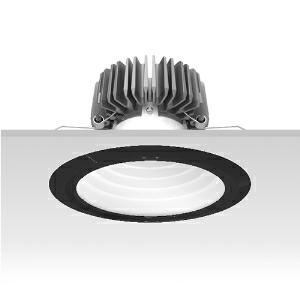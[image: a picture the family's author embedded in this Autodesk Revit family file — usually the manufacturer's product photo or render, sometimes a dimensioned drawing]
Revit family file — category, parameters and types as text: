
# Revit family: 3f_filippi_-_3f_reno_bianco_ampio_3f_filippi_-_30625_a01026_-_3f_reno_200_wh_2000-930_wide___vt_bk_0df5
name_source: partatom
category: Lighting Fixtures
units: mm (PartAtom-declared; Revit-internal decimal feet)

## family parameters
Cut with Voids When Loaded = No
Host = Face
Light Source = No
Part Type = Normal
Room Calculation Point = No
Round Connector Dimension = Use Diameter
Shared = No

## types (1)
- 3F Filippi - 3F Reno Bianco Ampio (1 x LED, 1804 lm, 24 W, 3000 K)
    Apparent Load = 24 VA
    Approval mark = CE
    CIE Flux Codes = 75 94 99 100 100
    Color Rendering = 90
    Color Temperature = 3000 K
    Control Gear = Electronic ballast
    Default Elevation = 1800 mm
    Description = ILLUMINOTECHNICAL
Luminous efficiency 100% (DLOR 100%, ULOR 0%).
Initial luminous flux of the luminaire 1804 lm.
Direct symmetric wide distribution.
Installation Interdistance Transv.D = 1.56 x hu - Long.D = 1.56 x hu.
Average luminance <3000 cd/m² for radial angles >65°.
Tabular UGR (CIE 117 - 4H-8H; S=0.25H; 70/50/20): RUG 20.6 - 20.5.
Beam angle: 74° - 74°.
Luminous efficacy 75 lm/W.
Lifetime (L90/B10): 30000 h. (tq+25°C)
Lifetime (L85/B10): 50000 h. (tq+25°C)
Lifetime (L70/B10): 80000 h. (tq+25°C)
Sudden decreased luminous flux after 50000 hours: 0% (C0).
Photobiological safety in compliance with IEC/TR 62778: RG0 risk exempt, (IEC 62471).
In compliance with IEC/EN 62722-2-1 - IEC/EN 62717 standards.

SOURCE
Compact LED module 2000/930.
Energy efficiency class (UE 2019/2020 - UE 2019/2015): E.
CIE 13.3 Colour rendering index: CRI >90 (R9 >50%).
IES TM-30 Fidelity Index: Rf = 92 Rg = 101.
CCT nominal colour temperature 3000 K.
Colour initial tolerance (MacAdam): SDCM 3.
Zhaga Book 3 compliant.

MECHANICAL
Passive heat dissipator in die-casting aluminium, oversized, for optimum thermal management of the LED module.
Parabolic element with graduated/concentric rings in white polycarbonate.
Transparent external lens with glossy and satin differentiated surfaces, with a cooling and anti-insect system in methacrylate (PMMA).
Fastening spring clips in stainless steel.
Dimensions: diameter 226 mm, height 146 mm. Weight 1.07 kg.
IP44 protection degree for exposed part, IP20 for recessed part.
Mechanical strength to impacts IK06 (1 joule).
Glow-wire test resistance 650°C.

ELECTRICAL
Wiring on a separate unit.
Halogen Free electronic wiring 230V-50/60Hz, power factor 0.95, THD <25%, constant output current, SELV, class II, 1 driver.
Power of the luminaire 24 W.
ENEC - CE.
SAFE FLICKER: PstLM=<1 and SVM=<0.4 (IEC TR 61547-1 and IEC TR 63158), to ensure a more comfortable and safe light.
Luminaire compliant with EN 60598-2-22 for power supply from a centralised emergency system CPSS (Central Power Supply System), not incorporated in the luminaire - high risk areas excluded. The default power and flux are 100% in AC and 100% in DC.
Ambient temperature from 0°C to +25°C.
Temperature class T6 max 85°C.
Relative humidity UR: <85%.

INSTALLATION
Pull-up recessed fitting.
False ceiling carving: 200 mm.
All accessories dedicated to this product are available on the Catalog and on our website www.3F-Filippi.com.

ACCESSORIES
A01026 - VT transparent glass, tempered, not flammable, locked and in line with the trim, in black polycarbonate.

APPLICATIONS
Environments: architectural, commercial, exhibition areas, transit areas, corridors, shops, display windows, service areas.
In false ceilings with narrow voids.

WARNING
Luminaire designed for disposal/recycling at end-of-life.
Replaceable (LED only) light source by a professional. Replaceable control gear by a professional.
    Height = 0 mm  [stored 0 ft]
    Lamp = 1 x LED
    Lamp Light Flux = 1804 lm
    Lamp Power = 24 W
    Lamp count = 1
    Length = 226 mm
    Lifetime = 50000 h
    Luminous efficacy = 75 lm/W
    Manufacturer = 3F Filippi
    ModVariant = No
    Model = 3F Filippi - 30625+A01026 - 3F Reno 200 WH 2000-930 WIDE + VT BK
    Mounting Place = Ceiling
    Mounting Type = Recessed
    Number of Poles = 1
    OnlyDefault = Yes
    Power Factor = 1
    Product Name = 3F Filippi - 3F Reno Bianco Ampio
    Product group = recessed luminaire
    ProductGroupID = 4
    Protection Class = Protection class II
    Protection Degree = IP 20
    RLX_Detail_Level = 1
    RLX_Emergency_Light_Flux = 0 lm
    RLX_Emergency_Type = 0
    RLX_Emergency_Type_DB = No
    RlxData = <blob elided: 99805 chars, md5=a5d1450b>
    Socket = socket
    Standby Power = 0 W
    System Light Flux = 1804 lm
    System Power = 24 W
    Type Comments = Product without accessories
    Type Image = 3ffilippi_3f_reno_200_wh__a01026.jpg
    URL = http://relux.com
    VarID = ---
    Voltage = 0 V
    Weight = 0.00 kg
    Width = 0 mm  [stored 0 ft]

note: [stored X ft] marks values corroborated as IEEE doubles in the binary element streams (Revit-internal decimal feet)

## geometry (parser evidence)
native form markers: Blend x4, Sweep x10
no freeform markers — native parametric forms only
